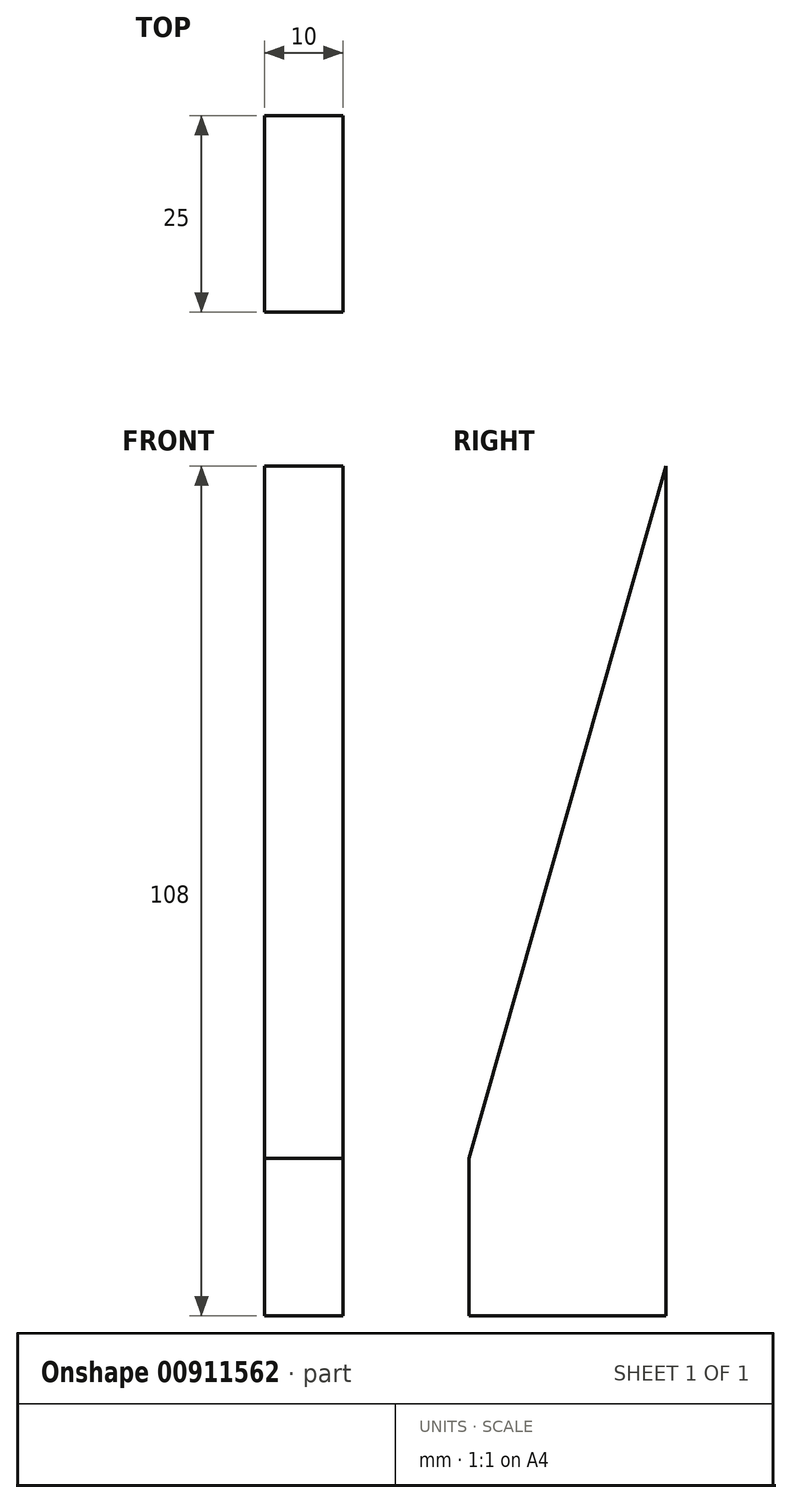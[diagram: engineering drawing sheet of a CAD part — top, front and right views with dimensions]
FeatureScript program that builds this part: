
annotation { "Feature Type Name" : "Feature", "Feature Type Description" : "" }
export const myFeature = defineFeature(function(context is Context, id is Id, definition is map)
    precondition{}
    {
        {
            var Q0;
            Q0=qCreatedBy(makeId("Right.planeOp"),FACE);
            var sketch = newSketch(context, id + "F0", { "sketchPlane" : qUnion([Q0])});
            skLineSegment(sketch, "E0", {"start": v(0, 0) * mm, "end": v(-25, 0) * mm});
            skLineSegment(sketch, "E1", {"start": v(-25, 0) * mm, "end": v(-25, 20) * mm});
            skLineSegment(sketch, "E2", {"start": v(0, 0) * mm, "end": v(0, 108) * mm});
            skLineSegment(sketch, "E3", {"start": v(-25, 20) * mm, "end": v(0, 108) * mm});
            skSolve(sketch);
        }
        {
            var Q0;
            Q0=makeQuery(id+"F0.imprint","IMPRINT",FACE,{"disambiguationData":[TD([[makeQuery(id+"F0.imprint","IMPRINT",EDGE,{"derivedFrom":sQuery(id+"F0.wireOp",EDGE,"E0")}),-1.0]])]});
            extrude(context, id + "F1", {"entities" : qUnion([Q0]), "depth" : 10 * mm, "offsetDistance" : 25 * mm});
        }
    });
